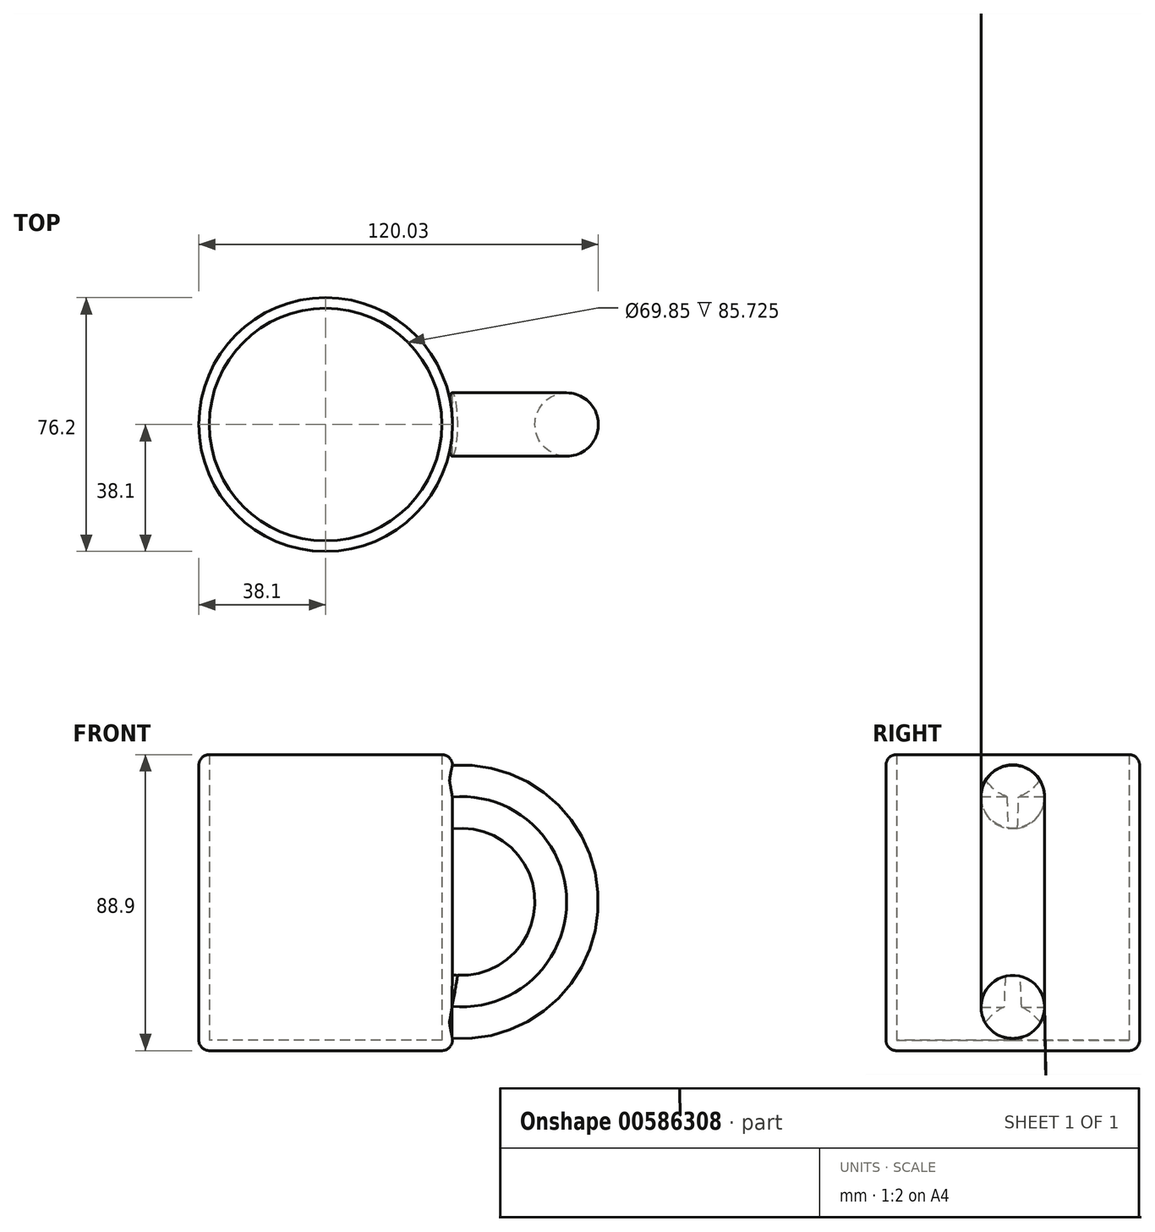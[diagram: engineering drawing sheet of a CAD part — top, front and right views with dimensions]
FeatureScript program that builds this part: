
annotation { "Feature Type Name" : "Feature", "Feature Type Description" : "" }
export const myFeature = defineFeature(function(context is Context, id is Id, definition is map)
    precondition{}
    {
        {
            var Q0;
            Q0=qCreatedBy(makeId("Top.planeOp"),FACE);
            var sketch = newSketch(context, id + "F0", { "sketchPlane" : qUnion([Q0])});
            skCircle(sketch, "E0", {"center": v(0, 0) * mm, "radius": 38.1 * mm});
            skSolve(sketch);
        }
        {
            var Q0;
            Q0=makeQuery(id+"F0.imprint","IMPRINT",FACE,{"disambiguationData":[TD([[makeQuery(id+"F0.imprint","IMPRINT",EDGE,{"derivedFrom":sQuery(id+"F0.wireOp",EDGE,"E0")}),1.0]])]});
            extrude(context, id + "F1", {"entities" : qUnion([Q0]), "depth" : 88.9 * mm, "offsetDistance" : 25.4 * mm});
        }
        {
            var Q0;
            Q0=makeQuery(id+"F1.opExtrude","CAP_FACE",FACE,{"disambiguationData":[OSD([sQuery(id+"F0.wireOp",EDGE,"E0")])],"isStart":false});
            shell(context, id + "F2", {"entities" : qUnion([Q0]), "thickness" : 3.17 * mm});
        }
        {
            var Q0;
            Q0=qCreatedBy(makeId("Right.planeOp"),FACE);
            cPlane(context, id + "F3", {"entities" : qUnion([Q0]), "cplaneType" : CPlaneType.OFFSET, "offset" : 38.1 * mm, "width" : 152.4 * mm, "height" : 152.4 * mm});
        }
        {
            var Q0;
            Q0=qCreatedBy(id+"F3.planeOp",FACE);
            var sketch = newSketch(context, id + "F4", { "sketchPlane" : qUnion([Q0])});
            skCircle(sketch, "E1", {"center": v(0, 76.13) * mm, "radius": 9.53 * mm});
            skCircle(sketch, "E2", {"center": v(0, 13.2) * mm, "radius": 9.53 * mm});
            skSolve(sketch);
        }
        {
            var Q0;
            Q0=qCreatedBy(makeId("Front.planeOp"),FACE);
            var sketch = newSketch(context, id + "F5", { "sketchPlane" : qUnion([Q0])});
            skArc(sketch, "E3", {"start": v(38, 13.08) * mm, "mid": v(72.57, 44.67) * mm, "end": v(38.06, 76.33) * mm});
            skSolve(sketch);
        }
        {
            var Q0;
            Q0=makeQuery(id+"F4.imprint","IMPRINT",FACE,{"disambiguationData":[TD([[makeQuery(id+"F4.imprint","IMPRINT",EDGE,{"derivedFrom":sQuery(id+"F4.wireOp",EDGE,"E1")}),1.0]])]});
            var Q1;
            Q1=makeQuery(id+"F4.imprint","IMPRINT",FACE,{"disambiguationData":[TD([[makeQuery(id+"F4.imprint","IMPRINT",EDGE,{"derivedFrom":sQuery(id+"F4.wireOp",EDGE,"E2")}),1.0]])]});
            var Q2;
            Q2=sQuery(id+"F5.wireOp",EDGE,"E3");
            sweep(context, id + "F6", {"operationType" : NewBodyOperationType.ADD, "profiles" : qUnion([Q0, Q1]), "path" : qUnion([Q2])});
        }
        {
            var Q0;
            Q0=makeQuery(id+"F1.opExtrude","CAP_EDGE",EDGE,{"disambiguationData":[OSD([sQuery(id+"F0.wireOp",EDGE,"E0")])],"isStart":false});
            var Q1;
            Q1=makeQuery(id+"F1.opExtrude","CAP_EDGE",EDGE,{"disambiguationData":[OSD([sQuery(id+"F0.wireOp",EDGE,"E0")])],"isStart":true});
            fillet(context, id + "F7", {"entities" : qUnion([Q0, Q1]), "radius" : 3.17 * mm, "tangentPropagation" : true, "allowEdgeOverflow" : false});
        }
    });
